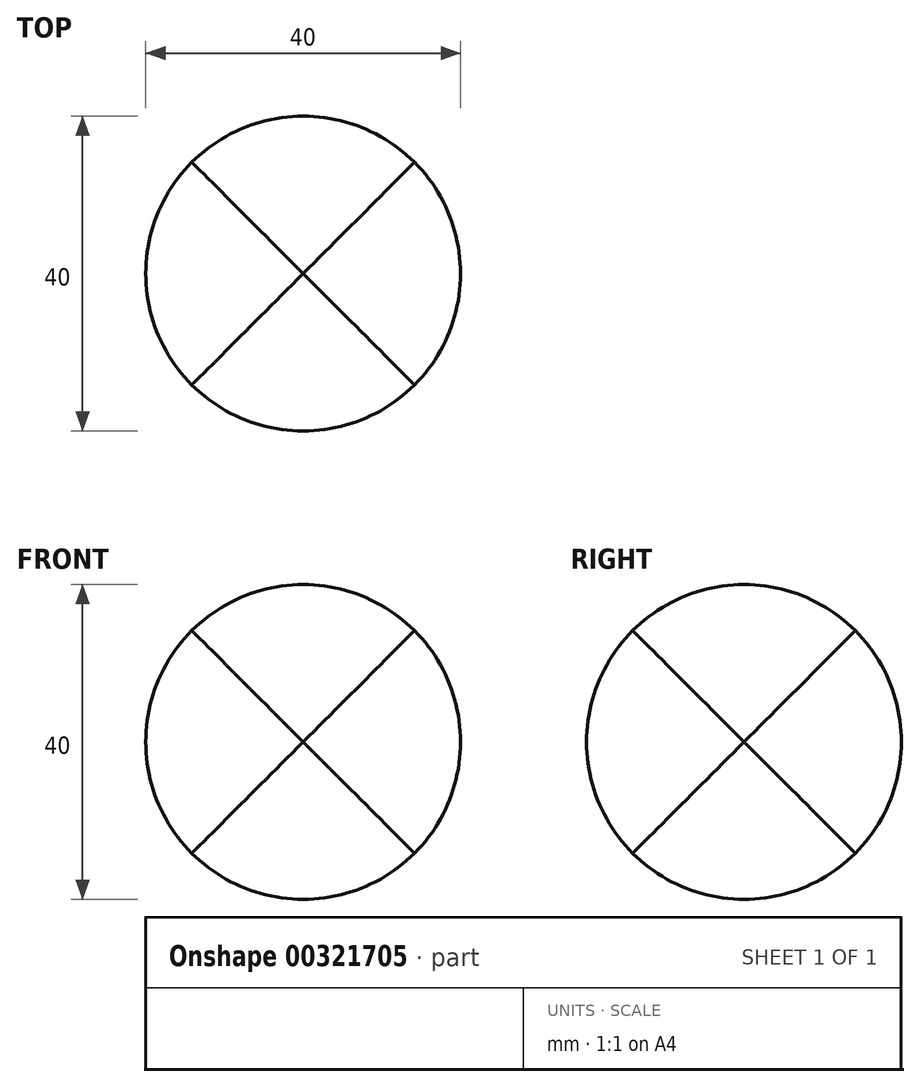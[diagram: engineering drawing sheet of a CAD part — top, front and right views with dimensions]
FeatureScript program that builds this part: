
annotation { "Feature Type Name" : "Feature", "Feature Type Description" : "" }
export const myFeature = defineFeature(function(context is Context, id is Id, definition is map)
    precondition{}
    {
        {
            var Q0;
            Q0=qCreatedBy(makeId("Front.planeOp"),FACE);
            var sketch = newSketch(context, id + "F0", { "sketchPlane" : qUnion([Q0])});
            skCircle(sketch, "E0", {"center": v(0, 0) * mm, "radius": 20 * mm});
            skSolve(sketch);
        }
        {
            var Q0;
            Q0=makeQuery(id+"F0.imprint","IMPRINT",FACE,{"disambiguationData":[TD([[makeQuery(id+"F0.imprint","IMPRINT",EDGE,{"derivedFrom":sQuery(id+"F0.wireOp",EDGE,"E0")}),1.0]])]});
            extrude(context, id + "F1", {"entities" : qUnion([Q0]), "endBound" : BoundingType.SYMMETRIC, "depth" : 50 * mm});
        }
        {
            var Q0;
            Q0=qCreatedBy(makeId("Right.planeOp"),FACE);
            var Q1;
            Q1=qCreatedBy(makeId("Front.planeOp"),FACE);
            cPlane(context, id + "F2", {"entities" : qUnion([Q0, Q1]), "cplaneType" : CPlaneType.MID_PLANE, "offset" : 25 * mm, "width" : 150 * mm, "height" : 150 * mm});
        }
        {
            var Q0;
            Q0=qCreatedBy(id+"F2.planeOp",FACE);
            var sketch = newSketch(context, id + "F3", { "sketchPlane" : qUnion([Q0])});
            skLineSegment(sketch, "E1", {"start": v(0, 0) * mm, "end": v(28.28, 20) * mm});
            skSolve(sketch);
        }
        {
            var Q0;
            Q0=makeQuery(id+"F1.opExtrude","SWEPT_BODY",BODY,{"disambiguationData":[OSD([sQuery(id+"F0.wireOp",EDGE,"E0")])]});
            var Q1;
            Q1=sQuery(id+"F3.wireOp",EDGE,"E1");
            circularPattern(context, id + "F4", {"entities" : qUnion([Q0]), "axis" : qUnion([Q1]), "angle" : 360 * degree, "instanceCount" : 3, "equalSpace" : true});
        }
        {
            var Q0;
            Q0=makeQuery(id+"F4.opPattern","COPY",BODY,{"derivedFrom":makeQuery(id+"F1.opExtrude","SWEPT_BODY",BODY,{"disambiguationData":[OSD([sQuery(id+"F0.wireOp",EDGE,"E0")])]}),"instanceName":"2"});
            var Q1;
            Q1=makeQuery(id+"F4.opPattern","COPY",BODY,{"derivedFrom":makeQuery(id+"F1.opExtrude","SWEPT_BODY",BODY,{"disambiguationData":[OSD([sQuery(id+"F0.wireOp",EDGE,"E0")])]}),"instanceName":"1"});
            var Q2;
            Q2=makeQuery(id+"F1.opExtrude","SWEPT_BODY",BODY,{"disambiguationData":[OSD([sQuery(id+"F0.wireOp",EDGE,"E0")])]});
            booleanBodies(context, id + "F5", {"operationType" : BooleanOperationType.INTERSECTION, "tools" : qUnion([Q0, Q1, Q2])});
        }
    });
